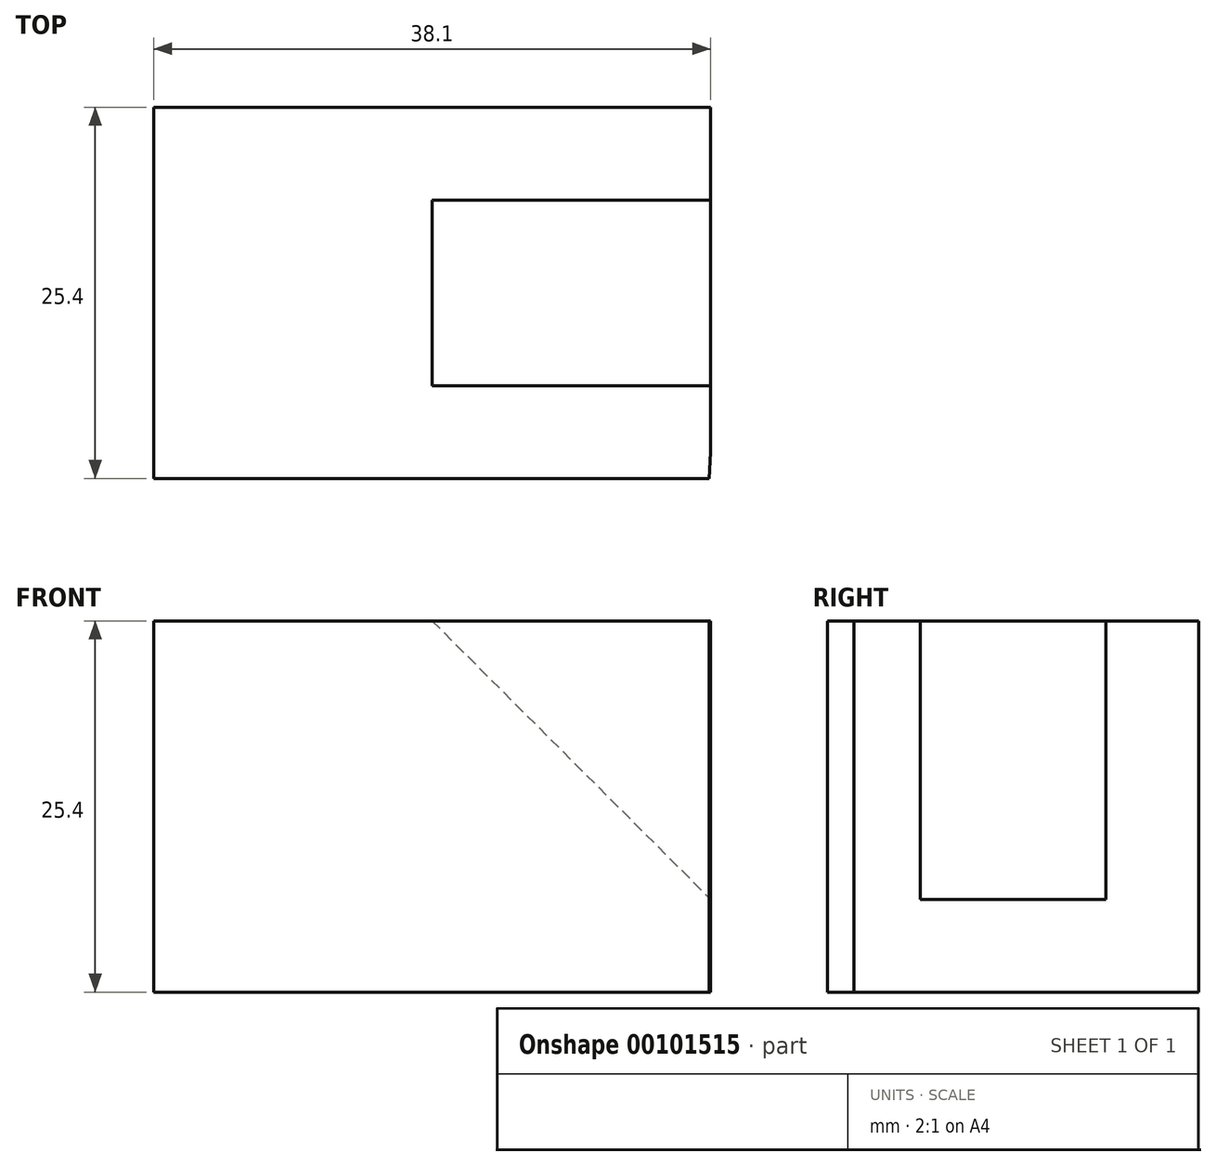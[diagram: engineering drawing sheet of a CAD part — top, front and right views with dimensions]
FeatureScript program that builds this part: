
annotation { "Feature Type Name" : "Feature", "Feature Type Description" : "" }
export const myFeature = defineFeature(function(context is Context, id is Id, definition is map)
    precondition{}
    {
        {
            var Q0;
            Q0=qCreatedBy(makeId("Front.planeOp"),FACE);
            var sketch = newSketch(context, id + "F0", { "sketchPlane" : qUnion([Q0])});
            skLineSegment(sketch, "E0.bottom", {"start": v(0, 0) * mm, "end": v(38.1, 0) * mm});
            skLineSegment(sketch, "E0.top", {"start": v(0, -25.4) * mm, "end": v(38.1, -25.4) * mm});
            skLineSegment(sketch, "E0.left", {"start": v(0, 0) * mm, "end": v(0, -25.4) * mm});
            skLineSegment(sketch, "E0.right", {"start": v(38.1, 0) * mm, "end": v(38.1, -25.4) * mm});
            skSolve(sketch);
        }
        {
            var Q0;
            Q0 = qSketchRegion(id + "F0", true);
            extrude(context, id + "F1", {"entities" : qUnion([Q0]), "depth" : 25.4 * mm});
        }
        {
            var Q0;
            Q0=qCreatedBy(makeId("Front.planeOp"),FACE);
            var sketch = newSketch(context, id + "F2", { "sketchPlane" : qUnion([Q0])});
            skLineSegment(sketch, "E1.bottom", {"start": v(0, 0) * mm, "end": v(38.1, 0) * mm});
            skLineSegment(sketch, "E1.top", {"start": v(0, -19.05) * mm, "end": v(38.1, -19.05) * mm});
            skLineSegment(sketch, "E1.left", {"start": v(0, 0) * mm, "end": v(0, -19.05) * mm});
            skLineSegment(sketch, "E1.right", {"start": v(38.1, 0) * mm, "end": v(38.1, -19.05) * mm});
            skLineSegment(sketch, "E2.bottom", {"start": v(0, 0) * mm, "end": v(19.05, 0) * mm});
            skLineSegment(sketch, "E2.top", {"start": v(0, -12.7) * mm, "end": v(19.05, -12.7) * mm});
            skLineSegment(sketch, "E2.left", {"start": v(0, 0) * mm, "end": v(0, -12.7) * mm});
            skLineSegment(sketch, "E2.right", {"start": v(19.05, 0) * mm, "end": v(19.05, -12.7) * mm});
            skLineSegment(sketch, "E3", {"start": v(19.05, 0) * mm, "end": v(38.1, -19.05) * mm});
            skLineSegment(sketch, "E4", {"start": v(38.1, -19.05) * mm, "end": v(38.1, 0) * mm});
            skLineSegment(sketch, "E5", {"start": v(38.1, 0) * mm, "end": v(19.05, 0) * mm});
            skSolve(sketch);
        }
        {
            var Q0;
            Q0=makeQuery(id+"F2.imprint","IMPRINT",FACE,{"disambiguationData":[TD([[makeQuery(id+"F2.imprint","IMPRINT",EDGE,{"derivedFrom":sQuery(id+"F2.wireOp",EDGE,"E3")}),1.0]])]});
            extrude(context, id + "F3", {"entities" : qUnion([Q0]), "operationType" : NewBodyOperationType.REMOVE, "endBound" : BoundingType.THROUGH_ALL, "depth" : 25.4 * mm});
        }
        {
            var Q0;
            Q0=qCreatedBy(makeId("Top.planeOp"),FACE);
            var sketch = newSketch(context, id + "F4", { "sketchPlane" : qUnion([Q0])});
            skLineSegment(sketch, "E6.bottom", {"start": v(0, 0) * mm, "end": v(19.05, 0) * mm});
            skLineSegment(sketch, "E6.top", {"start": v(0, -6.35) * mm, "end": v(19.05, -6.35) * mm});
            skLineSegment(sketch, "E6.left", {"start": v(0, 0) * mm, "end": v(0, -6.35) * mm});
            skLineSegment(sketch, "E6.right", {"start": v(19.05, 0) * mm, "end": v(19.05, -6.35) * mm});
            skLineSegment(sketch, "E7.top", {"start": v(0, -19.05) * mm, "end": v(19.05, -19.05) * mm});
            skLineSegment(sketch, "E7.left", {"start": v(0, 0) * mm, "end": v(0, -19.05) * mm});
            skLineSegment(sketch, "E7.right", {"start": v(19.05, 0) * mm, "end": v(19.05, -19.05) * mm});
            skLineSegment(sketch, "E8.bottom", {"start": v(19.05, -6.35) * mm, "end": v(39.93, -6.35) * mm});
            skLineSegment(sketch, "E8.top", {"start": v(19.05, 0) * mm, "end": v(39.93, 0) * mm});
            skLineSegment(sketch, "E8.left", {"start": v(19.05, -6.35) * mm, "end": v(19.05, 0) * mm});
            skLineSegment(sketch, "E8.right", {"start": v(39.93, -6.35) * mm, "end": v(39.93, 0) * mm});
            skLineSegment(sketch, "E9.bottom", {"start": v(19.05, -19.05) * mm, "end": v(39.93, -19.05) * mm});
            skLineSegment(sketch, "E9.top", {"start": v(19.05, -26.96) * mm, "end": v(39.93, -26.96) * mm});
            skLineSegment(sketch, "E9.left", {"start": v(19.05, -19.05) * mm, "end": v(19.05, -26.96) * mm});
            skLineSegment(sketch, "E9.right", {"start": v(39.93, -19.05) * mm, "end": v(39.93, -26.96) * mm});
            skSolve(sketch);
        }
        {
            var Q0;
            Q0=makeQuery(id+"F4.imprint","IMPRINT",FACE,{"disambiguationData":[TD([[makeQuery(id+"F4.imprint","IMPRINT",EDGE,{"derivedFrom":sQuery(id+"F4.wireOp",EDGE,"E9.bottom")}),-1.0]])]});
            var Q1;
            Q1=makeQuery(id+"F4.imprint","IMPRINT",FACE,{"disambiguationData":[TD([[makeQuery(id+"F4.imprint","IMPRINT",EDGE,{"derivedFrom":sQuery(id+"F4.wireOp",EDGE,"E8.bottom")}),1.0]])]});
            extrude(context, id + "F5", {"entities" : qUnion([Q0, Q1]), "operationType" : NewBodyOperationType.ADD, "oppositeDirection" : true, "depth" : 25.4 * mm});
        }
        {
            var Q0;
            Q0=qCreatedBy(makeId("Top.planeOp"),FACE);
            var sketch = newSketch(context, id + "F6", { "sketchPlane" : qUnion([Q0])});
            skLineSegment(sketch, "E10", {"start": v(0, 0) * mm, "end": v(0, -25.4) * mm});
            skLineSegment(sketch, "E11", {"start": v(0, -25.4) * mm, "end": v(38.1, -25.4) * mm});
            skLineSegment(sketch, "E12", {"start": v(38.1, -25.4) * mm, "end": v(38.1, 0) * mm});
            skLineSegment(sketch, "E13", {"start": v(38.1, 0) * mm, "end": v(39.82, 0) * mm});
            skLineSegment(sketch, "E14", {"start": v(39.82, 0) * mm, "end": v(39.82, -27.63) * mm});
            skLineSegment(sketch, "E15", {"start": v(39.82, -27.63) * mm, "end": v(18.32, -27.63) * mm});
            skLineSegment(sketch, "E16", {"start": v(18.32, -27.63) * mm, "end": v(18.32, -25.4) * mm});
            skSolve(sketch);
        }
        {
            var Q0;
            Q0 = qSketchRegion(id + "F6", true);
            extrude(context, id + "F7", {"entities" : qUnion([Q0]), "operationType" : NewBodyOperationType.REMOVE, "oppositeDirection" : true, "depth" : 25.4 * mm});
        }
        {
            var Q0;
            Q0=qCreatedBy(makeId("Front.planeOp"),FACE);
            var sketch = newSketch(context, id + "F8", { "sketchPlane" : qUnion([Q0])});
            skLineSegment(sketch, "E17.bottom", {"start": v(39.34, 0.84) * mm, "end": v(41.02, 0.84) * mm});
            skLineSegment(sketch, "E17.top", {"start": v(39.34, -26.7) * mm, "end": v(41.02, -26.7) * mm});
            skLineSegment(sketch, "E17.left", {"start": v(39.34, 0.84) * mm, "end": v(39.34, -26.7) * mm});
            skLineSegment(sketch, "E17.right", {"start": v(41.02, 0.84) * mm, "end": v(41.02, -26.7) * mm});
            skSolve(sketch);
        }
        {
            var Q0;
            Q0=makeQuery(id+"F8.imprint","IMPRINT",FACE,{"disambiguationData":[TD([[makeQuery(id+"F8.imprint","IMPRINT",EDGE,{"derivedFrom":sQuery(id+"F8.wireOp",EDGE,"E17.bottom")}),-1.0]])]});
            extrude(context, id + "F9", {"entities" : qUnion([Q0]), "operationType" : NewBodyOperationType.REMOVE, "endBound" : BoundingType.THROUGH_ALL, "depth" : 25.4 * mm, "hasDraft" : true, "draftAngle" : 3 * degree});
        }
        {
            var Q0;
            Q0=qCreatedBy(makeId("Front.planeOp"),FACE);
            var sketch = newSketch(context, id + "F10", { "sketchPlane" : qUnion([Q0])});
            skLineSegment(sketch, "E18.bottom", {"start": v(38.82, 0) * mm, "end": v(41.3, 0) * mm});
            skLineSegment(sketch, "E18.top", {"start": v(38.82, -25.9) * mm, "end": v(41.3, -25.9) * mm});
            skLineSegment(sketch, "E18.left", {"start": v(38.82, 0) * mm, "end": v(38.82, -25.9) * mm});
            skLineSegment(sketch, "E18.right", {"start": v(41.3, 0) * mm, "end": v(41.3, -25.9) * mm});
            skSolve(sketch);
        }
        {
            var Q0;
            Q0 = qSketchRegion(id + "F10", true);
            extrude(context, id + "F11", {"entities" : qUnion([Q0]), "operationType" : NewBodyOperationType.REMOVE, "endBound" : BoundingType.THROUGH_ALL, "depth" : 25.4 * mm});
        }
    });
